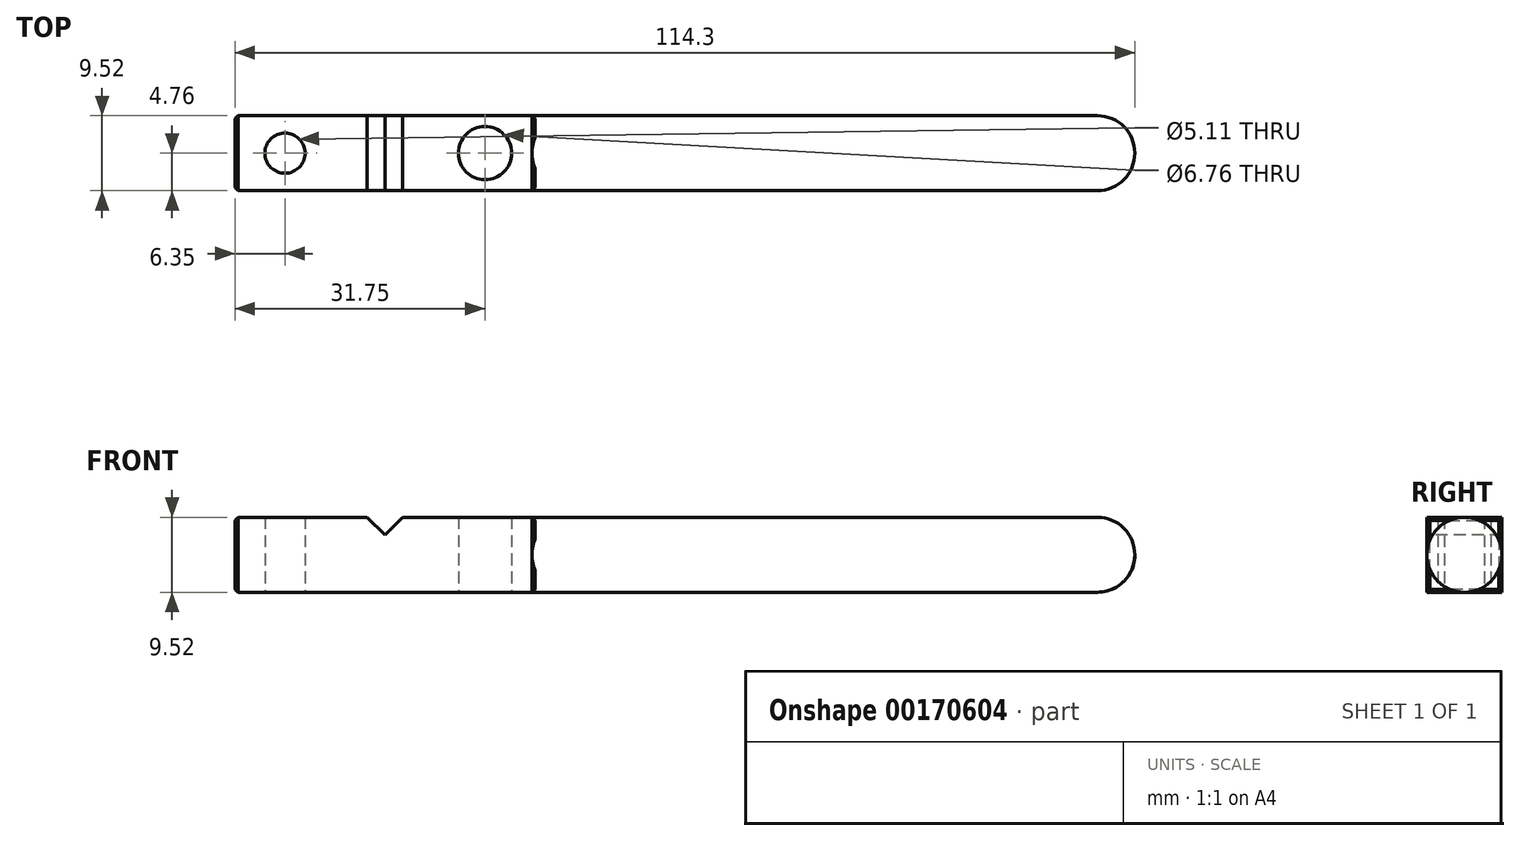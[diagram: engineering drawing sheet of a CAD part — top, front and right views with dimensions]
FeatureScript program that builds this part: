
annotation { "Feature Type Name" : "Feature", "Feature Type Description" : "" }
export const myFeature = defineFeature(function(context is Context, id is Id, definition is map)
    precondition{}
    {
        {
            var Q0;
            Q0=qCreatedBy(makeId("Top.planeOp"),FACE);
            var sketch = newSketch(context, id + "F0", { "sketchPlane" : qUnion([Q0])});
            skLineSegment(sketch, "E0.bottom", {"start": v(-19.05, -4.76) * mm, "end": v(19.05, -4.76) * mm});
            skLineSegment(sketch, "E0.top", {"start": v(-19.05, 4.76) * mm, "end": v(19.05, 4.76) * mm});
            skLineSegment(sketch, "E0.left", {"start": v(-19.05, -4.76) * mm, "end": v(-19.05, 4.76) * mm});
            skLineSegment(sketch, "E0.right", {"start": v(19.05, -4.76) * mm, "end": v(19.05, 4.76) * mm});
            skSolve(sketch);
        }
        {
            var Q0;
            Q0=makeQuery(id+"F0.imprint","IMPRINT",FACE,{"disambiguationData":[TD([[makeQuery(id+"F0.imprint","IMPRINT",EDGE,{"derivedFrom":sQuery(id+"F0.wireOp",EDGE,"E0.bottom")}),1.0]])]});
            extrude(context, id + "F1", {"entities" : qUnion([Q0]), "depth" : 9.52 * mm, "symmetric" : true});
        }
        {
            var Q0;
            Q0=makeQuery(id+"F1.opExtrude","SWEPT_FACE",FACE,{"disambiguationData":[OSD([sQuery(id+"F0.wireOp",EDGE,"E0.right")])]});
            var sketch = newSketch(context, id + "F2", { "sketchPlane" : qUnion([Q0])});
            skCircle(sketch, "E1", {"center": v(0, 0) * mm, "radius": 4.76 * mm});
            skSolve(sketch);
        }
        {
            var Q0;
            {var subQ0=sQuery(id+"F2.wireOp",EDGE,"E1");var subQ1=sQuery(id+"F0.wireOp",EDGE,"E0.right");var subQ2=makeQuery(id+"F2.imprint","INTERSECT",VERTEX,{"derivedFrom":[makeQuery(id+"F1.opExtrude","CAP_EDGE",EDGE,{"disambiguationData":[OSD([subQ1])],"isStart":false}),subQ0]});Q0=makeQuery(id+"F2.imprint","IMPRINT",FACE,{"disambiguationData":[TD([[makeQuery(id+"F2.imprint","IMPRINT",EDGE,{"disambiguationData":[TD([[subQ2,1.0]])],"derivedFrom":subQ0}),1.0]])]});}
            extrude(context, id + "F3", {"entities" : qUnion([Q0]), "operationType" : NewBodyOperationType.ADD, "depth" : 76.2 * mm});
        }
        {
            var Q0;
            Q0=makeQuery(id+"F3.opExtrude","CAP_EDGE",EDGE,{"disambiguationData":[OSD([sQuery(id+"F2.wireOp",EDGE,"E1")])],"isStart":false});
            fillet(context, id + "F4", {"entities" : qUnion([Q0]), "radius" : 4.76 * mm, "tangentPropagation" : true, "allowEdgeOverflow" : false});
        }
        {
            var Q0;
            Q0=makeQuery(id+"F1.opExtrude","CAP_FACE",FACE,{"disambiguationData":[OSD([sQuery(id+"F0.wireOp",EDGE,"E0.bottom"),sQuery(id+"F0.wireOp",EDGE,"E0.top"),sQuery(id+"F0.wireOp",EDGE,"E0.left"),sQuery(id+"F0.wireOp",EDGE,"E0.right")])],"isStart":false});
            var sketch = newSketch(context, id + "F5", { "sketchPlane" : qUnion([Q0])});
            skCircle(sketch, "E2", {"center": v(-12.7, 0) * mm, "radius": 3.73 * mm});
            skCircle(sketch, "E3", {"center": v(12.7, 0) * mm, "radius": 4.05 * mm});
            skSolve(sketch);
        }
        {
            var Q0;
            Q0=sQuery(id+"F5.wireOp",VERTEX,"E2.center");
            var Q1;
            Q1=makeQuery(id+"F1.opExtrude","SWEPT_BODY",BODY,{"disambiguationData":[OSD([sQuery(id+"F0.wireOp",EDGE,"E0.bottom"),sQuery(id+"F0.wireOp",EDGE,"E0.top"),sQuery(id+"F0.wireOp",EDGE,"E0.left"),sQuery(id+"F0.wireOp",EDGE,"E0.right")])]});
            hole(context, id + "F6", {"style" : HoleStyle.SIMPLE, "endStyle" : HoleEndStyle.THROUGH, "standardTappedOrClearance" : lookupTablePath({ "standard" : "ANSI", "engagement" : "75%", "pitch" : "20 tpi", "size" : "1/4", "type" : "Tapped" }), "standardBlindInLast" : lookupTablePath({ "standard" : "ANSI", "engagement" : "75%", "pitch" : "20 tpi", "size" : "1/4", "type" : "Tapped" }), "holeDiameter" : 5.1 * mm, "startFromSketch" : true, "locations" : qUnion([Q0]), "scope" : qUnion([Q1]), "isTappedThrough" : true, "majorDiameter" : 6.35 * mm, "showTappedDepth" : true});
        }
        {
            var Q0;
            Q0=makeQuery(id+"F1.opExtrude","CAP_FACE",FACE,{"disambiguationData":[OSD([sQuery(id+"F0.wireOp",EDGE,"E0.bottom"),sQuery(id+"F0.wireOp",EDGE,"E0.top"),sQuery(id+"F0.wireOp",EDGE,"E0.left"),sQuery(id+"F0.wireOp",EDGE,"E0.right")])],"isStart":false});
            var sketch = newSketch(context, id + "F7", { "sketchPlane" : qUnion([Q0])});
            skCircle(sketch, "E4", {"center": v(12.7, 0) * mm, "radius": 2.56 * mm});
            skSolve(sketch);
        }
        {
            var Q0;
            Q0=sQuery(id+"F7.wireOp",VERTEX,"E4.center");
            var Q1;
            Q1=makeQuery(id+"F1.opExtrude","SWEPT_BODY",BODY,{"disambiguationData":[OSD([sQuery(id+"F0.wireOp",EDGE,"E0.bottom"),sQuery(id+"F0.wireOp",EDGE,"E0.top"),sQuery(id+"F0.wireOp",EDGE,"E0.left"),sQuery(id+"F0.wireOp",EDGE,"E0.right")])]});
            hole(context, id + "F8", {"style" : HoleStyle.SIMPLE, "endStyle" : HoleEndStyle.THROUGH, "standardTappedOrClearance" : lookupTablePath({ "standard" : "ANSI", "fit" : "Normal (ASME)", "size" : "1/4", "type" : "Clearance" }), "standardBlindInLast" : lookupTablePath({ "fit" : "Free", "standard" : "ANSI", "size" : "1/4", "type" : "Clearance" }), "holeDiameter" : 6.76 * mm, "startFromSketch" : true, "locations" : qUnion([Q0]), "scope" : qUnion([Q1]), "isTappedThrough" : true});
        }
        {
            var Q0;
            Q0=makeQuery(id+"F1.opExtrude","SWEPT_FACE",FACE,{"disambiguationData":[OSD([sQuery(id+"F0.wireOp",EDGE,"E0.bottom")])]});
            var sketch = newSketch(context, id + "F9", { "sketchPlane" : qUnion([Q0])});
            skLineSegment(sketch, "E5", {"start": v(0, 2.52) * mm, "end": v(-2.25, 4.76) * mm});
            skLineSegment(sketch, "E6", {"start": v(0, 2.52) * mm, "end": v(2.25, 4.76) * mm});
            skSolve(sketch);
        }
        {
            var Q0;
            {var subQ0=sQuery(id+"F9.wireOp",EDGE,"E5");Q0=makeQuery(id+"F9.imprint","IMPRINT",FACE,{"disambiguationData":[TD([[makeQuery(id+"F9.imprint","IMPRINT",EDGE,{"derivedFrom":subQ0}),-1.0]])]});}
            extrude(context, id + "F10", {"entities" : qUnion([Q0]), "operationType" : NewBodyOperationType.REMOVE, "oppositeDirection" : true, "depth" : 25.4 * mm});
        }
        {
            var Q0;
            Q0=makeQuery(id+"F6.hole-0.boolean.opBoolean","COPY",EDGE,{"derivedFrom":makeQuery(id+"F6.hole-0.opRevolve","SWEPT_EDGE",EDGE,{"disambiguationData":[OSD([sQuery(id+"F6.hole-0.sketch.wireOp",EDGE,"core_line_2"),sQuery(id+"F6.hole-0.sketch.wireOp",EDGE,"core_line_3")])]})});
            var Q1;
            Q1=makeQuery(id+"F8.hole-0.boolean.opBoolean","COPY",EDGE,{"derivedFrom":makeQuery(id+"F8.hole-0.opRevolve","SWEPT_EDGE",EDGE,{"disambiguationData":[OSD([sQuery(id+"F8.hole-0.sketch.wireOp",EDGE,"core_line_2"),sQuery(id+"F8.hole-0.sketch.wireOp",EDGE,"core_line_3")])]})});
            var Q2;
            Q2=makeQuery(id+"F6.hole-0.boolean.opBoolean","INTERSECT",EDGE,{"derivedFrom":[makeQuery(id+"F1.opExtrude","CAP_FACE",FACE,{"disambiguationData":[OSD([sQuery(id+"F0.wireOp",EDGE,"E0.bottom"),sQuery(id+"F0.wireOp",EDGE,"E0.top"),sQuery(id+"F0.wireOp",EDGE,"E0.left"),sQuery(id+"F0.wireOp",EDGE,"E0.right")])],"isStart":true}),makeQuery(id+"F6.hole-0.opRevolve","SWEPT_FACE",FACE,{"disambiguationData":[OSD([sQuery(id+"F6.hole-0.sketch.wireOp",EDGE,"core_line_2")])]})]});
            var Q3;
            Q3=makeQuery(id+"F8.hole-0.boolean.opBoolean","INTERSECT",EDGE,{"derivedFrom":[makeQuery(id+"F1.opExtrude","CAP_FACE",FACE,{"disambiguationData":[OSD([sQuery(id+"F0.wireOp",EDGE,"E0.bottom"),sQuery(id+"F0.wireOp",EDGE,"E0.top"),sQuery(id+"F0.wireOp",EDGE,"E0.left"),sQuery(id+"F0.wireOp",EDGE,"E0.right")])],"isStart":true}),makeQuery(id+"F8.hole-0.opRevolve","SWEPT_FACE",FACE,{"disambiguationData":[OSD([sQuery(id+"F8.hole-0.sketch.wireOp",EDGE,"core_line_2")])]})]});
            var Q4;
            {var subQ0=sQuery(id+"F0.wireOp",EDGE,"E0.right");var subQ1=sQuery(id+"F0.wireOp",EDGE,"E0.top");Q4=makeQuery(id+"F3.boolean.opBoolean","SPLIT",EDGE,{"disambiguationData":[TD([makeQuery(id+"F1.opExtrude","CAP_FACE",FACE,{"disambiguationData":[OSD([sQuery(id+"F0.wireOp",EDGE,"E0.bottom"),subQ1,sQuery(id+"F0.wireOp",EDGE,"E0.left"),subQ0])],"isStart":true})])],"derivedFrom":makeQuery(id+"F1.opExtrude","SWEPT_EDGE",EDGE,{"disambiguationData":[OSD([subQ1,subQ0])]})});}
            var Q5;
            {var subQ0=sQuery(id+"F0.wireOp",EDGE,"E0.right");var subQ1=sQuery(id+"F0.wireOp",EDGE,"E0.top");Q5=makeQuery(id+"F3.boolean.opBoolean","SPLIT",EDGE,{"disambiguationData":[TD([makeQuery(id+"F1.opExtrude","SWEPT_FACE",FACE,{"disambiguationData":[OSD([subQ1])]})])],"derivedFrom":makeQuery(id+"F1.opExtrude","CAP_EDGE",EDGE,{"disambiguationData":[OSD([subQ0])],"isStart":false})});}
            var Q6;
            {var subQ0=sQuery(id+"F0.wireOp",EDGE,"E0.right");var subQ1=sQuery(id+"F0.wireOp",EDGE,"E0.top");Q6=makeQuery(id+"F3.boolean.opBoolean","SPLIT",EDGE,{"disambiguationData":[TD([makeQuery(id+"F1.opExtrude","SWEPT_FACE",FACE,{"disambiguationData":[OSD([subQ1])]})])],"derivedFrom":makeQuery(id+"F1.opExtrude","CAP_EDGE",EDGE,{"disambiguationData":[OSD([subQ0])],"isStart":true})});}
            var Q7;
            {var subQ0=sQuery(id+"F0.wireOp",EDGE,"E0.bottom");var subQ1=sQuery(id+"F0.wireOp",EDGE,"E0.right");Q7=makeQuery(id+"F3.boolean.opBoolean","SPLIT",EDGE,{"disambiguationData":[TD([makeQuery(id+"F1.opExtrude","CAP_FACE",FACE,{"disambiguationData":[OSD([subQ0,sQuery(id+"F0.wireOp",EDGE,"E0.top"),sQuery(id+"F0.wireOp",EDGE,"E0.left"),subQ1])],"isStart":false})])],"derivedFrom":makeQuery(id+"F1.opExtrude","SWEPT_EDGE",EDGE,{"disambiguationData":[OSD([subQ0,subQ1])]})});}
            var Q8;
            Q8=makeQuery(id+"F1.opExtrude","SWEPT_FACE",FACE,{"disambiguationData":[OSD([sQuery(id+"F0.wireOp",EDGE,"E0.left")])]});
            chamfer(context, id + "F11", {"entities" : qUnion([Q0, Q1, Q2, Q3, Q4, Q5, Q6, Q7, Q8]), "width" : 0.38 * mm, "tangentPropagation" : true});
        }
    });
